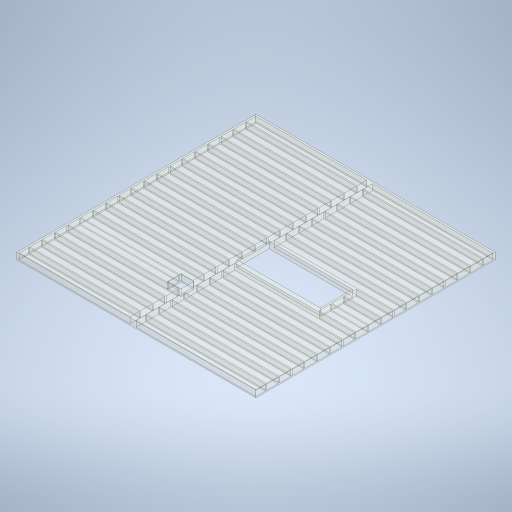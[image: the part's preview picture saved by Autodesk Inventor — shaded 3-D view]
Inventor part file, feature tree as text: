
AUTODESK INVENTOR PART (.ipt)
format: ipt  version: 2024 (Build 280153000, 153)  size: 547,328 bytes
history: native  units: in
note: dims shown in document units (in); Inventor stores cm internally (conversion verified against a paired STEP export)
features: extrude x7, sketch x7
ambient origin geometry x8: Origin, YZ Plane, XZ Plane, XY Plane, X Axis, Y Axis, Z Axis, Center Point
bodies: Solid1 (feature_tree)
feature tree (14):
  extrude  "Extrusion1"  Depth=300.0in
  extrude  "Extrusion2"  Depth=1.5in
  extrude  "Extrusion3"  Depth=140.5in
  extrude  "Extrusion4"  Depth=13.25in
  extrude  "Extrusion8"  Depth=13.25in
  extrude  "Extrusion9"  Depth=16.0in
  extrude  "Extrusion10"  Depth=125.5in
  sketch  "Sketch1"  dims[d1=300.0in d3=300.0in]
  sketch  "Sketch2"  dims[d5=7.5in d6=0.0in d9=1.5in]
  sketch  "Sketch3"  dims[d10=7.5in d11=140.5in]
  sketch  "Sketch4"  dims[d12=1.5in d13=13.25in]
  sketch  "Sketch8"  dims[d14=7.0866in d16=16.0in d17=0.3937in d19=1.0in d21=13.25in]
  sketch  "Sketch9"  dims[d22=0.75in d23=0.0in d25=16.0in]
  sketch  "Sketch10"  dims[d26=16.0in d27=125.5in d28=63.0in d29=0.75in d30=0.0in d32=104.75in d33=129.75in d34=40.5in d35=0.0in d36=0.0in d45=153.75in d46=1.5in d47=7.5in d48=0.0in d49=1.0in d50=0.0in d51=1.5in d52=7.5in d53=0.0in d38=0.5in d39=0.0344in d40=0.5in d41=0.0344in]
